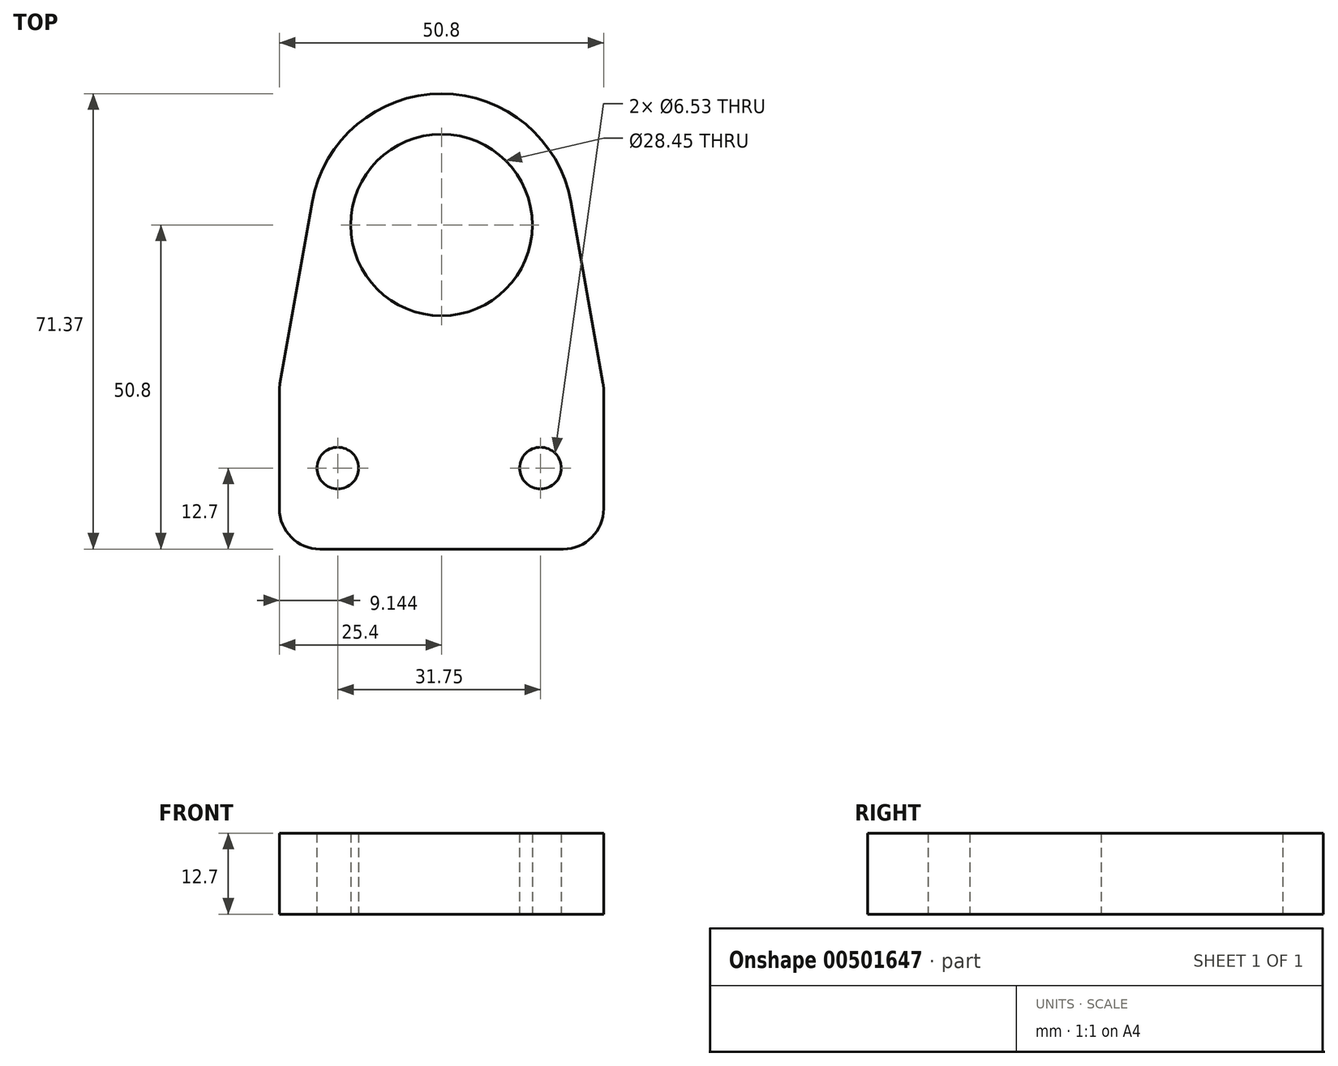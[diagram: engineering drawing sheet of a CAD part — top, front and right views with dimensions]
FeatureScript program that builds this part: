
annotation { "Feature Type Name" : "Feature", "Feature Type Description" : "" }
export const myFeature = defineFeature(function(context is Context, id is Id, definition is map)
    precondition{}
    {
        {
            var Q0;
            Q0=qCreatedBy(makeId("Top.planeOp"),FACE);
            var sketch = newSketch(context, id + "F0", { "sketchPlane" : qUnion([Q0])});
            skLineSegment(sketch, "E0.bottom", {"start": v(19.05, -12.7) * mm, "end": v(-19.05, -12.7) * mm});
            skLineSegment(sketch, "E0.left", {"start": v(25.4, -6.35) * mm, "end": v(25.4, 12.7) * mm});
            skLineSegment(sketch, "E0.right", {"start": v(-25.4, -6.35) * mm, "end": v(-25.4, 12.7) * mm});
            skPoint(sketch, "E0.middle", {"position": v(0, 0) * mm});
            skLineSegment(sketch, "E1", {"start": v(0, 0) * mm, "end": v(0, -12.7) * mm, "construction": true});
            skLineSegment(sketch, "E2", {"start": v(-25.4, 0) * mm, "end": v(25.4, 0) * mm, "construction": true});
            skPoint(sketch, "E3", {"position": v(-16.26, 0) * mm});
            skPoint(sketch, "E4", {"position": v(15.5, 0) * mm});
            skCircle(sketch, "E5", {"center": v(-16.26, 0) * mm, "radius": 3.26 * mm});
            skCircle(sketch, "E6", {"center": v(15.5, 0) * mm, "radius": 3.26 * mm});
            skCircle(sketch, "E7", {"center": v(0, 38.1) * mm, "radius": 14.22 * mm});
            skArc(sketch, "E8", {"start": v(20.26, 41.7) * mm, "mid": v(0, 58.67) * mm, "end": v(-20.26, 41.7) * mm});
            skLineSegment(sketch, "E9", {"start": v(-20.26, 41.7) * mm, "end": v(-25.4, 12.7) * mm});
            skLineSegment(sketch, "E10.MirrorCS", {"start": v(20.26, 41.7) * mm, "end": v(25.4, 12.7) * mm});
            skPoint(sketch, "E11.visualSharp", {"position": v(-25.4, -12.7) * mm});
            skArc(sketch, "E11.filletArc", {"start": v(-25.4, -6.35) * mm, "mid": v(-23.54, -10.84) * mm, "end": v(-19.05, -12.7) * mm});
            skPoint(sketch, "E12.visualSharp", {"position": v(25.4, -12.7) * mm});
            skArc(sketch, "E12.filletArc", {"start": v(19.05, -12.7) * mm, "mid": v(23.54, -10.84) * mm, "end": v(25.4, -6.35) * mm});
            skLineSegment(sketch, "E13", {"start": v(-25.4, 12.7) * mm, "end": v(25.4, 12.7) * mm, "construction": true});
            skSolve(sketch);
        }
        {
            var Q0;
            Q0=makeQuery(id+"F0.imprint","IMPRINT",FACE,{"disambiguationData":[TD([[makeQuery(id+"F0.imprint","IMPRINT",EDGE,{"derivedFrom":sQuery(id+"F0.wireOp",EDGE,"E0.bottom")}),-1.0]])]});
            extrude(context, id + "F1", {"entities" : qUnion([Q0]), "depth" : 12.7 * mm, "offsetDistance" : 25.4 * mm});
        }
        {
            var Q0;
            Q0=makeQuery(id+"F1.opExtrude","SWEPT_EDGE",EDGE,{"disambiguationData":[OSD([sQuery(id+"F0.wireOp",EDGE,"E0.left"),sQuery(id+"F0.wireOp",EDGE,"E10.MirrorCS")])]});
            var Q1;
            Q1=makeQuery(id+"F1.opExtrude","SWEPT_EDGE",EDGE,{"disambiguationData":[OSD([sQuery(id+"F0.wireOp",EDGE,"E0.right"),sQuery(id+"F0.wireOp",EDGE,"E9")])]});
            fillet(context, id + "F2", {"entities" : qUnion([Q0, Q1]), "radius" : 6.35 * mm, "tangentPropagation" : true, "allowEdgeOverflow" : false});
        }
    });
